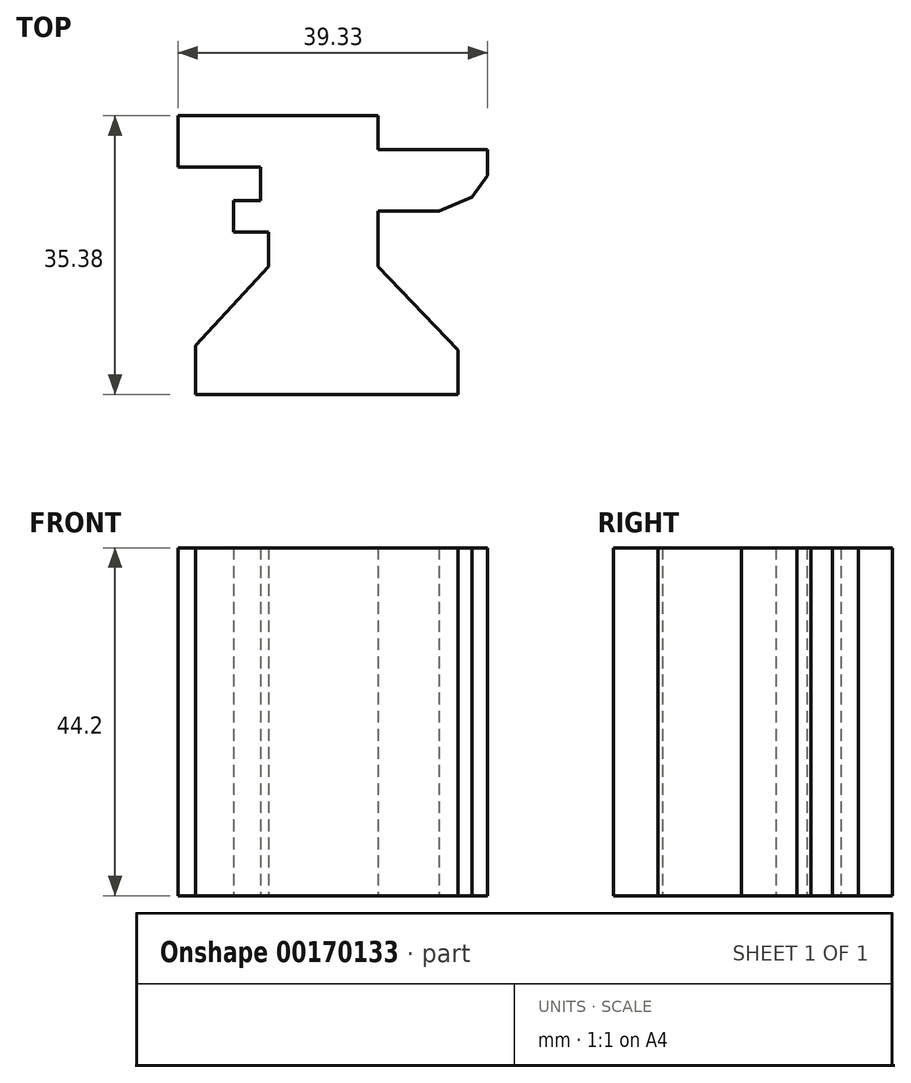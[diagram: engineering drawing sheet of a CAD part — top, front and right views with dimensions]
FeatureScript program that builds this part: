
annotation { "Feature Type Name" : "Feature", "Feature Type Description" : "" }
export const myFeature = defineFeature(function(context is Context, id is Id, definition is map)
    precondition{}
    {
        {
            var Q0;
            Q0=qCreatedBy(makeId("Top.planeOp"),FACE);
            var sketch = newSketch(context, id + "F0", { "sketchPlane" : qUnion([Q0])});
            skLineSegment(sketch, "E0", {"start": v(-17.4, 9) * mm, "end": v(-17.4, 14.74) * mm});
            skLineSegment(sketch, "E1", {"start": v(-17.4, 14.74) * mm, "end": v(8, 14.74) * mm});
            skLineSegment(sketch, "E2", {"start": v(8, 14.74) * mm, "end": v(8, 10.43) * mm});
            skLineSegment(sketch, "E3", {"start": v(8, 10.43) * mm, "end": v(21.92, 10.43) * mm});
            skLineSegment(sketch, "E4", {"start": v(21.92, 10.43) * mm, "end": v(21.92, 7.16) * mm});
            skLineSegment(sketch, "E5", {"start": v(21.92, 7.16) * mm, "end": v(19.94, 4.44) * mm});
            skLineSegment(sketch, "E6", {"start": v(19.94, 4.44) * mm, "end": v(15.75, 2.64) * mm});
            skLineSegment(sketch, "E7", {"start": v(15.75, 2.64) * mm, "end": v(8, 2.64) * mm});
            skLineSegment(sketch, "E8", {"start": v(8, 2.64) * mm, "end": v(8, -4.42) * mm});
            skLineSegment(sketch, "E9", {"start": v(8, -4.42) * mm, "end": v(18.13, -15.03) * mm});
            skLineSegment(sketch, "E10", {"start": v(18.13, -15.03) * mm, "end": v(18.13, -20.64) * mm});
            skLineSegment(sketch, "E11", {"start": v(18.13, -20.64) * mm, "end": v(-15.16, -20.64) * mm});
            skLineSegment(sketch, "E12", {"start": v(-15.16, -20.64) * mm, "end": v(-15.16, -14.45) * mm});
            skLineSegment(sketch, "E13", {"start": v(-15.16, -14.45) * mm, "end": v(-5.9, -4.42) * mm});
            skLineSegment(sketch, "E14", {"start": v(-5.9, -4.42) * mm, "end": v(-5.9, 0) * mm});
            skLineSegment(sketch, "E15", {"start": v(-5.9, 0) * mm, "end": v(-10.38, 0) * mm});
            skLineSegment(sketch, "E16", {"start": v(-10.38, 0) * mm, "end": v(-10.38, 3.94) * mm});
            skLineSegment(sketch, "E17", {"start": v(-10.38, 3.94) * mm, "end": v(-6.94, 3.94) * mm});
            skLineSegment(sketch, "E18", {"start": v(-6.94, 3.94) * mm, "end": v(-6.94, 8.25) * mm});
            skLineSegment(sketch, "E19", {"start": v(-6.94, 8.25) * mm, "end": v(-17.4, 8.25) * mm});
            skLineSegment(sketch, "E20", {"start": v(-17.4, 8.25) * mm, "end": v(-17.4, 9) * mm});
            skSolve(sketch);
        }
        {
            var Q0;
            Q0=makeQuery(id+"F0.imprint","IMPRINT",FACE,{"disambiguationData":[TD([[makeQuery(id+"F0.imprint","IMPRINT",EDGE,{"derivedFrom":sQuery(id+"F0.wireOp",EDGE,"E0")}),-1.0]])]});
            extrude(context, id + "F1", {"entities" : qUnion([Q0]), "depth" : 44.2 * mm});
        }
    });
